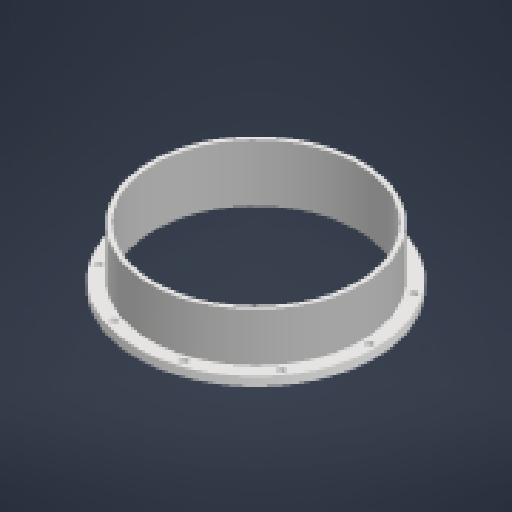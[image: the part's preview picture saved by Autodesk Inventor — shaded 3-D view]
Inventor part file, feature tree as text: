
AUTODESK INVENTOR PART (.ipt)
format: ipt  version: 2025 (Build 290162000, 162)  size: 337,920 bytes
history: native  units: in
note: dims shown in document units (in); Inventor stores cm internally (conversion verified against a paired STEP export)
features: sketch x8, extrude x7, other x3
ambient origin geometry x8: Origin, YZ Plane, XZ Plane, XY Plane, X Axis, Y Axis, Z Axis, Center Point
bodies: Body1 (feature_tree)
feature tree (18):
  other  "Cylinder.ipt"
  extrude  "Extrusion1"  Depth=0.3937in
  extrude  "Extrusion2"  Depth=0.3937in TaperAngle=0.0deg
  sketch  "Sketch3"  dims[d15=0.1969in d16=0.0in d17=10.6299in]
  extrude  "Extrusion3"  Depth=10.6299in
  extrude  "Extrusion5"  Depth=0.1969in TaperAngle=0.0deg
  sketch  "Sketch6"  dims[d20=3.937in d22=360.0deg d24=0.1969in d25=0.0in]
  extrude  "Extrusion6"  Depth=10.6299in
  extrude  "Extrusion7"  Depth=0.3346in
  extrude  "Extrusion8"  Depth=0.1969in TaperAngle=0.0deg
  other  "Solid12::Cylinder.ipt"
  other  "TaggingFeature1"
  sketch  "Sketch1"  dims[d0=0.3937in d2=10.2362in]
  sketch  "Sketch2"  dims[d7=11.2205in d8=10.6299in]
  sketch  "Sketch5"  dims[d18=0.2953in d19=0.3346in]
  sketch  "Sketch Circular Pattern1"  dims[d3=0.0in d4=0.0in d5=0.3937in d6=0.0in]
  sketch  "Sketch Circular Pattern2"  dims[d9=10.6299in d10=0.1969in d11=0.0in]
  sketch  "Sketch7"  dims[d27=3.937in d29=360.0deg d31=0.0in d32=0.0in d33=2.1654in d34=0.0in d35=10.0394in d36=10.6299in d37=0.1969in]
